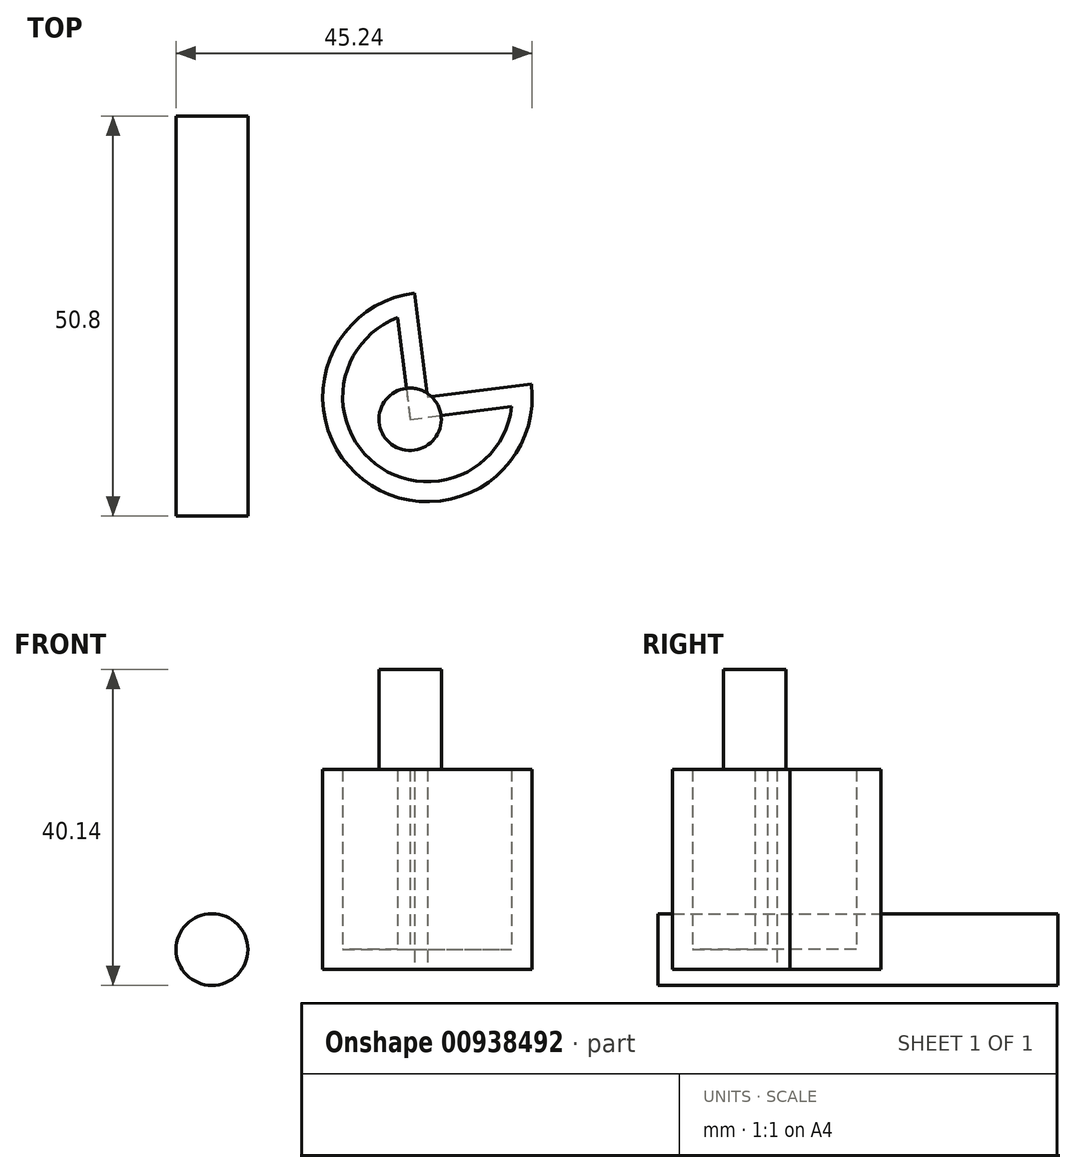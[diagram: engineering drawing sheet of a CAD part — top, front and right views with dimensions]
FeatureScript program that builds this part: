
annotation { "Feature Type Name" : "Feature", "Feature Type Description" : "" }
export const myFeature = defineFeature(function(context is Context, id is Id, definition is map)
    precondition{}
    {
        {
            var Q0;
            Q0=qCreatedBy(makeId("Top.planeOp"),FACE);
            var sketch = newSketch(context, id + "F0", { "sketchPlane" : qUnion([Q0])});
            skLineSegment(sketch, "E0", {"start": v(-128.54, 8.16) * mm, "end": v(-123.12, -35.69) * mm});
            skLineSegment(sketch, "E1", {"start": v(-123.12, -35.69) * mm, "end": v(-76.33, -29.9) * mm});
            skLineSegment(sketch, "E2", {"start": v(-76.33, -29.9) * mm, "end": v(-93.47, -32.02) * mm});
            skCircle(sketch, "E3", {"center": v(-123.12, -35.69) * mm, "radius": 13.3 * mm});
            skSolve(sketch);
        }
        {
            var Q0;
            {var subQ0=sQuery(id+"F0.wireOp",EDGE,"E1");var subQ1=sQuery(id+"F0.wireOp",EDGE,"E0");var subQ2=makeQuery(id+"F0.imprint","INTERSECT",VERTEX,{"derivedFrom":[subQ1,subQ0]});Q0=makeQuery(id+"F0.imprint","IMPRINT",FACE,{"disambiguationData":[TD([[makeQuery(id+"F0.imprint","IMPRINT",EDGE,{"disambiguationData":[TD([[subQ2,1.0]])],"derivedFrom":subQ1}),-1.0]])]});}
            extrude(context, id + "F1", {"entities" : qUnion([Q0]), "depth" : 25.4 * mm, "offsetDistance" : 25.4 * mm});
        }
        {
            var Q0;
            Q0=makeQuery(id+"F1.opExtrude","CAP_FACE",FACE,{"disambiguationData":[OSD([sQuery(id+"F0.wireOp",EDGE,"E0"),sQuery(id+"F0.wireOp",EDGE,"E1"),sQuery(id+"F0.wireOp",EDGE,"E3")])],"isStart":false});
            shell(context, id + "F2", {"entities" : qUnion([Q0]), "thickness" : 2.54 * mm});
        }
        {
            var Q0;
            Q0=makeQuery(id+"F1.opExtrude","CAP_FACE",FACE,{"disambiguationData":[OSD([sQuery(id+"F0.wireOp",EDGE,"E0"),sQuery(id+"F0.wireOp",EDGE,"E1"),sQuery(id+"F0.wireOp",EDGE,"E3")])],"isStart":false});
            var sketch = newSketch(context, id + "F3", { "sketchPlane" : qUnion([Q0])});
            skCircle(sketch, "E4", {"center": v(-125.33, -38.52) * mm, "radius": 3.96 * mm});
            skSolve(sketch);
        }
        {
            var Q0;
            Q0 = qSketchRegion(id + "F3", true);
            extrude(context, id + "F4", {"entities" : qUnion([Q0]), "operationType" : NewBodyOperationType.ADD, "depth" : 12.7 * mm, "offsetDistance" : 25.4 * mm});
        }
        {
            var Q0;
            Q0=qCreatedBy(makeId("Front.planeOp"),FACE);
            var sketch = newSketch(context, id + "F5", { "sketchPlane" : qUnion([Q0])});
            skCircle(sketch, "E5", {"center": v(-150.5, 2.52) * mm, "radius": 4.56 * mm});
            skSolve(sketch);
        }
        {
            var Q0;
            Q0=makeQuery(id+"F5.imprint","IMPRINT",FACE,{"disambiguationData":[TD([[makeQuery(id+"F5.imprint","IMPRINT",EDGE,{"derivedFrom":sQuery(id+"F5.wireOp",EDGE,"E5")}),1.0]])]});
            extrude(context, id + "F6", {"entities" : qUnion([Q0]), "operationType" : NewBodyOperationType.ADD, "depth" : 50.8 * mm, "offsetDistance" : 25.4 * mm});
        }
    });
